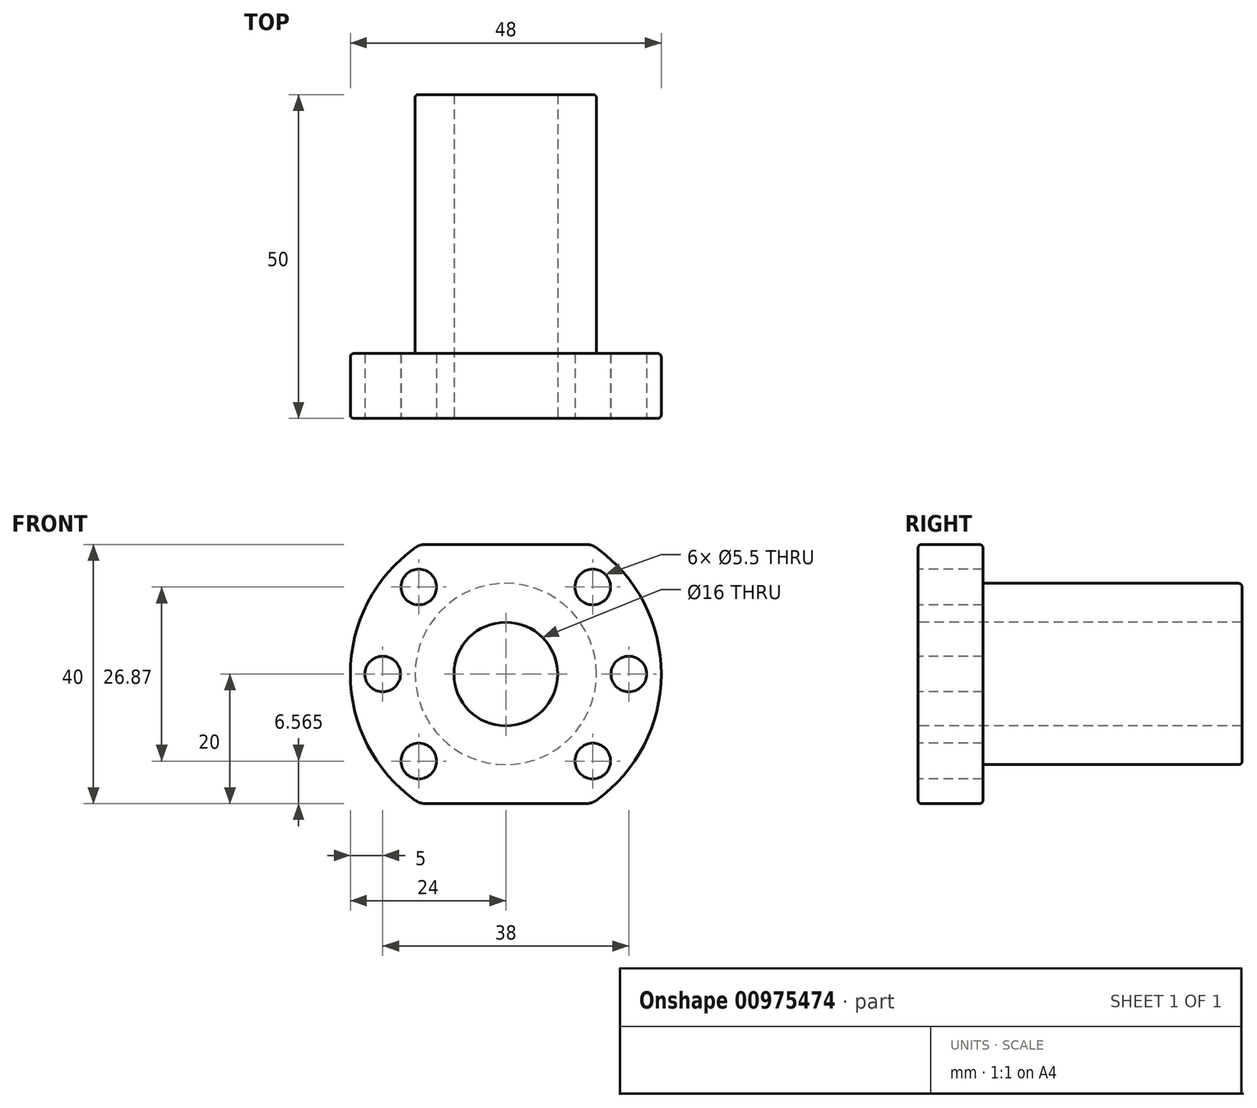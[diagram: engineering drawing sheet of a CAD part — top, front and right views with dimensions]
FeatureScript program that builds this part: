
annotation { "Feature Type Name" : "Feature", "Feature Type Description" : "" }
export const myFeature = defineFeature(function(context is Context, id is Id, definition is map)
    precondition{}
    {
        {
            var Q0;
            Q0=qCreatedBy(makeId("Front.planeOp"),FACE);
            var sketch = newSketch(context, id + "F0", { "sketchPlane" : qUnion([Q0])});
            skCircle(sketch, "E0", {"center": v(0, 0) * mm, "radius": 4 * mm});
            skCircle(sketch, "E1", {"center": v(0, 0) * mm, "radius": 5 * mm});
            skCircle(sketch, "E2", {"center": v(0, 0) * mm, "radius": 8 * mm});
            skSolve(sketch);
        }
        {
            var Q0;
            Q0=qCreatedBy(makeId("Front.planeOp"),FACE);
            var sketch = newSketch(context, id + "F1", { "sketchPlane" : qUnion([Q0])});
            skCircle(sketch, "E3.0", {"center": v(0, 0) * mm, "radius": 8 * mm});
            skArc(sketch, "E4", {"start": v(-13.27, 20) * mm, "mid": v(-24, 0) * mm, "end": v(-13.27, -20) * mm});
            skCircle(sketch, "E5", {"center": v(0, 0) * mm, "radius": 14 * mm});
            skCircle(sketch, "E6", {"center": v(-19, 0) * mm, "radius": 2.75 * mm});
            skCircle(sketch, "E7.1.0", {"center": v(-13.44, -13.44) * mm, "radius": 2.75 * mm});
            skCircle(sketch, "E7.1.1", {"center": v(0, 0) * mm, "radius": 19 * mm, "construction": true});
            skCircle(sketch, "E7.2.0", {"center": v(0, -19) * mm, "radius": 2.75 * mm, "construction": true});
            skCircle(sketch, "E7.2.1", {"center": v(0, 0) * mm, "radius": 19 * mm, "construction": true});
            skCircle(sketch, "E7.3.0", {"center": v(13.44, -13.44) * mm, "radius": 2.75 * mm});
            skCircle(sketch, "E7.4.0", {"center": v(19, 0) * mm, "radius": 2.75 * mm});
            skCircle(sketch, "E7.4.1", {"center": v(0, 0) * mm, "radius": 19 * mm, "construction": true});
            skCircle(sketch, "E7.5.0", {"center": v(13.44, 13.44) * mm, "radius": 2.75 * mm});
            skCircle(sketch, "E7.5.1", {"center": v(0, 0) * mm, "radius": 19 * mm, "construction": true});
            skCircle(sketch, "E7.6.0", {"center": v(0, 19) * mm, "radius": 2.75 * mm, "construction": true});
            skCircle(sketch, "E7.6.1", {"center": v(0, 0) * mm, "radius": 19 * mm, "construction": true});
            skCircle(sketch, "E7.7.0", {"center": v(-13.44, 13.44) * mm, "radius": 2.75 * mm});
            skCircle(sketch, "E7.7.1", {"center": v(0, 0) * mm, "radius": 19 * mm, "construction": true});
            skLineSegment(sketch, "E8.bottom", {"start": v(-13.27, 20) * mm, "end": v(13.27, 20) * mm});
            skLineSegment(sketch, "E8.top", {"start": v(-13.27, -20) * mm, "end": v(13.27, -20) * mm});
            skArc(sketch, "E9.trimOffspring", {"start": v(13.27, -20) * mm, "mid": v(24, 0) * mm, "end": v(13.27, 20) * mm});
            skSolve(sketch);
        }
        {
            var Q0;
            Q0=makeQuery(id+"F1.imprint","IMPRINT",FACE,{"disambiguationData":[TD([[makeQuery(id+"F1.imprint","IMPRINT",EDGE,{"derivedFrom":sQuery(id+"F1.wireOp",EDGE,"E3.0")}),-1.0]])]});
            extrude(context, id + "F2", {"entities" : qUnion([Q0]), "oppositeDirection" : true, "offsetDistance" : 25 * mm, "depth" : 50 * mm});
        }
        {
            var Q0;
            Q0=makeQuery(id+"F1.imprint","IMPRINT",FACE,{"disambiguationData":[TD([[makeQuery(id+"F1.imprint","IMPRINT",EDGE,{"derivedFrom":sQuery(id+"F1.wireOp",EDGE,"E5")}),-1.0]])]});
            extrude(context, id + "F3", {"entities" : qUnion([Q0]), "operationType" : NewBodyOperationType.ADD, "oppositeDirection" : true, "offsetDistance" : 25 * mm, "depth" : 10 * mm});
        }
        {
            var Q0;
            {var subQ0=sQuery(id+"F1.wireOp",EDGE,"E4");var subQ1=sQuery(id+"F1.wireOp",EDGE,"E8.bottom");Q0=makeQuery(id+"F3.opExtrude","SWEPT_EDGE",EDGE,{"disambiguationData":[OSD([subQ0,subQ1]),TDD([makeQuery(id+"F1.imprint","INTERSECT",VERTEX,{"disambiguationData":[OD(1.0)],"derivedFrom":[subQ0,subQ1]})])]});}
            var Q1;
            {var subQ0=sQuery(id+"F1.wireOp",EDGE,"E4");var subQ1=sQuery(id+"F1.wireOp",EDGE,"E8.bottom");Q1=makeQuery(id+"F3.opExtrude","SWEPT_EDGE",EDGE,{"disambiguationData":[OSD([subQ0,subQ1]),TDD([makeQuery(id+"F1.imprint","INTERSECT",VERTEX,{"disambiguationData":[OD(0.0)],"derivedFrom":[subQ0,subQ1]})])]});}
            var Q2;
            {var subQ0=sQuery(id+"F1.wireOp",EDGE,"E4");var subQ1=sQuery(id+"F1.wireOp",EDGE,"E8.top");Q2=makeQuery(id+"F3.opExtrude","SWEPT_EDGE",EDGE,{"disambiguationData":[OSD([subQ0,subQ1]),TDD([makeQuery(id+"F1.imprint","INTERSECT",VERTEX,{"disambiguationData":[OD(1.0)],"derivedFrom":[subQ0,subQ1]})])]});}
            var Q3;
            {var subQ0=sQuery(id+"F1.wireOp",EDGE,"E4");var subQ1=sQuery(id+"F1.wireOp",EDGE,"E8.top");Q3=makeQuery(id+"F3.opExtrude","SWEPT_EDGE",EDGE,{"disambiguationData":[OSD([subQ0,subQ1]),TDD([makeQuery(id+"F1.imprint","INTERSECT",VERTEX,{"disambiguationData":[OD(0.0)],"derivedFrom":[subQ0,subQ1]})])]});}
            var Q4;
            Q4=makeQuery(id+"F3.opExtrude","SWEPT_EDGE",EDGE,{"disambiguationData":[OSD([sQuery(id+"F1.wireOp",EDGE,"E8.bottom"),sQuery(id+"F1.wireOp",EDGE,"E9.trimOffspring")])]});
            var Q5;
            Q5=makeQuery(id+"F3.opExtrude","SWEPT_EDGE",EDGE,{"disambiguationData":[OSD([sQuery(id+"F1.wireOp",EDGE,"E8.top"),sQuery(id+"F1.wireOp",EDGE,"E9.trimOffspring")])]});
            fillet(context, id + "F4", {"entities" : qUnion([Q0, Q1, Q2, Q3, Q4, Q5]), "radius" : 2.5 * mm, "tangentPropagation" : true, "allowEdgeOverflow" : false});
        }
        {
            var Q0;
            Q0=makeQuery(id+"F3.opExtrude","CAP_EDGE",EDGE,{"disambiguationData":[OSD([sQuery(id+"F1.wireOp",EDGE,"E9.trimOffspring")])],"isStart":false});
            var Q1;
            Q1=makeQuery(id+"F3.opExtrude","CAP_EDGE",EDGE,{"disambiguationData":[OSD([sQuery(id+"F1.wireOp",EDGE,"E9.trimOffspring")])],"isStart":true});
            var Q2;
            Q2=makeQuery(id+"F3.opExtrude","CAP_EDGE",EDGE,{"disambiguationData":[OSD([sQuery(id+"F1.wireOp",EDGE,"E5")])],"isStart":false});
            var Q3;
            Q3=makeQuery(id+"F2.opExtrude","CAP_EDGE",EDGE,{"disambiguationData":[OSD([sQuery(id+"F1.wireOp",EDGE,"E5")])],"isStart":false});
            fillet(context, id + "F5", {"entities" : qUnion([Q0, Q1, Q2, Q3]), "radius" : 0.5 * mm, "tangentPropagation" : true, "allowEdgeOverflow" : false});
        }
    });
